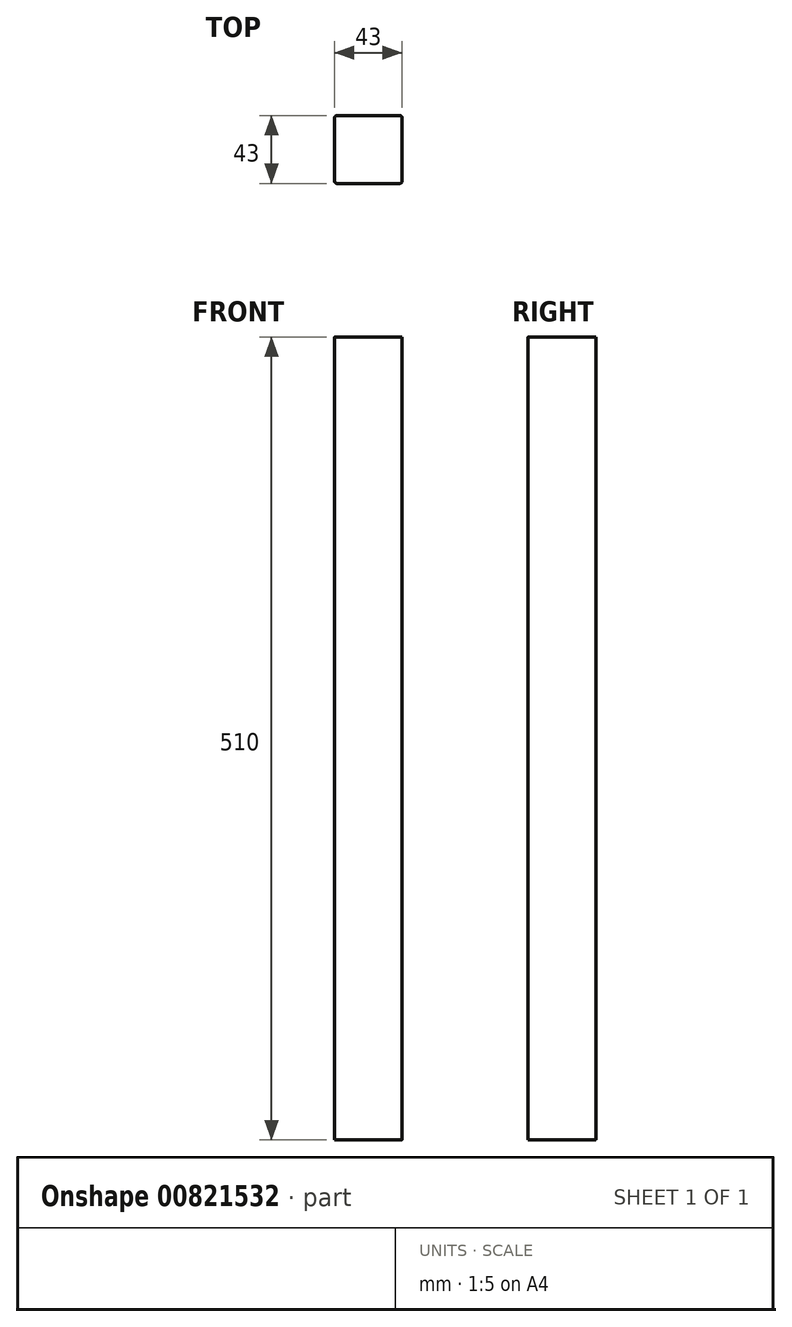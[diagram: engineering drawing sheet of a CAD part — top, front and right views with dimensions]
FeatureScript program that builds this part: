
annotation { "Feature Type Name" : "Feature", "Feature Type Description" : "" }
export const myFeature = defineFeature(function(context is Context, id is Id, definition is map)
    precondition{}
    {
        {
            var Q0;
            Q0=qCreatedBy(makeId("Top.planeOp"),FACE);
            var sketch = newSketch(context, id + "F0", { "sketchPlane" : qUnion([Q0])});
            skLineSegment(sketch, "E0.bottom", {"start": v(-21.5, 21.5) * mm, "end": v(21.5, 21.5) * mm});
            skLineSegment(sketch, "E0.top", {"start": v(-21.5, -21.5) * mm, "end": v(21.5, -21.5) * mm});
            skLineSegment(sketch, "E0.left", {"start": v(-21.5, 21.5) * mm, "end": v(-21.5, -21.5) * mm});
            skLineSegment(sketch, "E0.right", {"start": v(21.5, 21.5) * mm, "end": v(21.5, -21.5) * mm});
            skPoint(sketch, "E0.middle", {"position": v(0, 0) * mm});
            skSolve(sketch);
        }
        {
            var Q0;
            Q0=makeQuery(id+"F0.imprint","IMPRINT",FACE,{"disambiguationData":[TD([[makeQuery(id+"F0.imprint","IMPRINT",EDGE,{"derivedFrom":sQuery(id+"F0.wireOp",EDGE,"E0.bottom")}),-1.0]])]});
            extrude(context, id + "F1", {"entities" : qUnion([Q0]), "endBound" : BoundingType.SYMMETRIC, "depth" : (250 + 180 + 80) * mm, "offsetDistance" : 25 * mm});
        }
        {
            var Q0;
            Q0=makeQuery(id+"F1.opExtrude","SWEPT_EDGE",EDGE,{"disambiguationData":[OSD([sQuery(id+"F0.wireOp",EDGE,"E0.top"),sQuery(id+"F0.wireOp",EDGE,"E0.right")])]});
            var Q1;
            Q1=makeQuery(id+"F1.opExtrude","SWEPT_EDGE",EDGE,{"disambiguationData":[OSD([sQuery(id+"F0.wireOp",EDGE,"E0.bottom"),sQuery(id+"F0.wireOp",EDGE,"E0.right")])]});
            var Q2;
            Q2=makeQuery(id+"F1.opExtrude","SWEPT_EDGE",EDGE,{"disambiguationData":[OSD([sQuery(id+"F0.wireOp",EDGE,"E0.top"),sQuery(id+"F0.wireOp",EDGE,"E0.left")])]});
            var Q3;
            Q3=makeQuery(id+"F1.opExtrude","SWEPT_EDGE",EDGE,{"disambiguationData":[OSD([sQuery(id+"F0.wireOp",EDGE,"E0.bottom"),sQuery(id+"F0.wireOp",EDGE,"E0.left")])]});
            fillet(context, id + "F2", {"entities" : qUnion([Q0, Q1, Q2, Q3]), "radius" : 1.5 * mm, "tangentPropagation" : true, "allowEdgeOverflow" : false});
        }
    });
